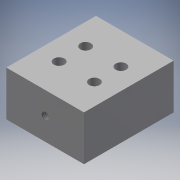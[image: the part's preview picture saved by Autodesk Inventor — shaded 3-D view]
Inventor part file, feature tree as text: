
AUTODESK INVENTOR PART (.ipt)
format: ipt  version: 2016 (Build 200138000, 138)  size: 130,048 bytes
history: native  units: mm (DEFAULTED — no unit token found)
features: sketch x4, extrude x2, hole x2
ambient origin geometry x8: Origin, YZ Plane, XZ Plane, XY Plane, X Axis, Y Axis, Z Axis, Center Point
bodies: Solid1 (feature_tree)
feature tree (8):
  extrude  "Extrusion1"  Depth=44.0mm
  hole  "Hole1"  [1 undecoded]
  extrude  "Extrusion2"  Depth=5.0mm
  sketch  "Sketch2"  dims[d0=50.8mm d1=44.0mm]
  sketch  "Sketch3"  dims[d2=25.4mm d3=0.0mm]
  hole  "Hole2"  [1 undecoded]
  sketch  "Sketch5"  dims[d11=6.0mm d12=6.0mm d13=6.0mm d14=6.0mm d15=20.0mm d16=15.0mm d18=0.0mm d19=5.0mm d20=6.0mm d21=20.594885mm d22=90.0deg d23=2.0mm d24=4.0mm d25=8.0mm d26=3.5mm d27=1.0mm d28=1.0mm]
  sketch  "Sketch4"  dims[d4=4.134mm d5=10.0mm d6=4.0mm d7=2.0mm d8=90.0deg d9=19.05mm d10=20.594885mm]
note: 2 required parameter values undecoded (feature->parameter linkage not recoverable at this tier; creation-order binding heuristic only, values carry confidence <= 0.55)
